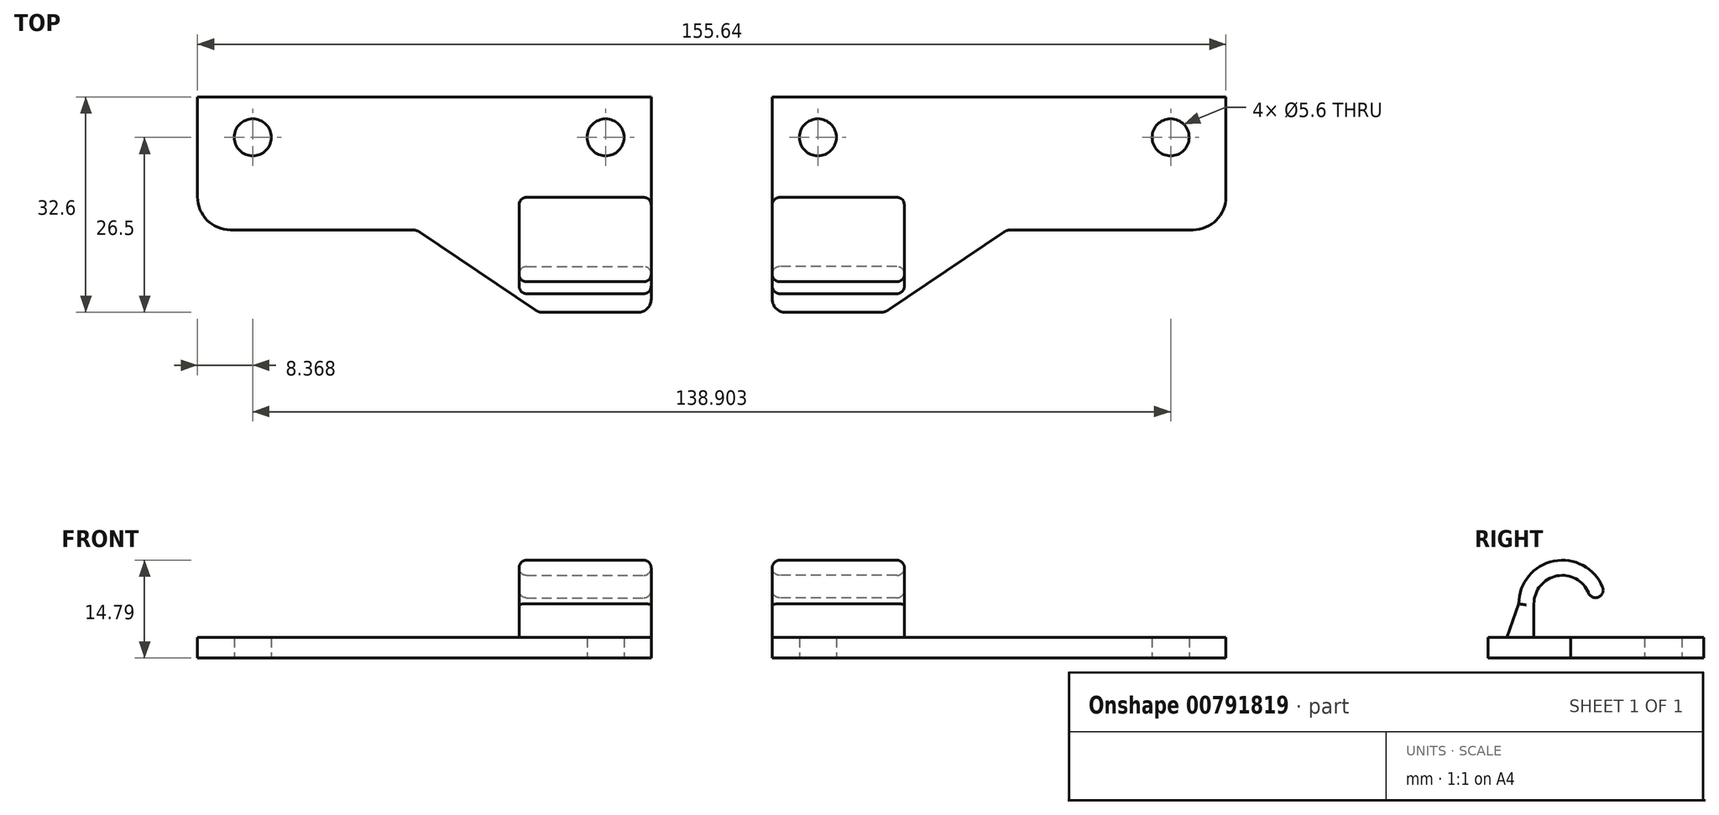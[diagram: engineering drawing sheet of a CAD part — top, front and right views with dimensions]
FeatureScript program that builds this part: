
annotation { "Feature Type Name" : "Feature", "Feature Type Description" : "" }
export const myFeature = defineFeature(function(context is Context, id is Id, definition is map)
    precondition{}
    {
        {
            var Q0;
            Q0=qCreatedBy(makeId("Top.planeOp"),FACE);
            var sketch = newSketch(context, id + "F0", { "sketchPlane" : qUnion([Q0])});
            skCircle(sketch, "E0", {"center": v(-17.35, 21.4) * mm, "radius": 2.8 * mm});
            skLineSegment(sketch, "E1", {"start": v(36.74, 27.5) * mm, "end": v(36.74, 21.3) * mm});
            skCircle(sketch, "E2", {"center": v(36.04, 21.4) * mm, "radius": 2.8 * mm});
            skPoint(sketch, "E3.visualSharp", {"position": v(-25.72, 27.5) * mm});
            skPoint(sketch, "E4.visualSharp", {"position": v(42.94, 27.5) * mm});
            skLineSegment(sketch, "E5", {"start": v(-25.72, 27.5) * mm, "end": v(-25.72, 22.5) * mm});
            skLineSegment(sketch, "E6", {"start": v(-20.72, 27.5) * mm, "end": v(-25.72, 27.5) * mm});
            skPoint(sketch, "E7.visualSharp", {"position": v(-25.72, 7.4) * mm});
            skArc(sketch, "E7.filletArc", {"start": v(-25.72, 12.4) * mm, "mid": v(-24.26, 8.86) * mm, "end": v(-20.72, 7.4) * mm});
            skLineSegment(sketch, "E8", {"start": v(37.94, 27.5) * mm, "end": v(42.94, 27.5) * mm});
            skLineSegment(sketch, "E9", {"start": v(42.94, 22.5) * mm, "end": v(42.94, 27.5) * mm});
            skLineSegment(sketch, "E10", {"start": v(42.94, 7.4) * mm, "end": v(42.94, -3.1) * mm});
            skLineSegment(sketch, "E11", {"start": v(26.55, -5.1) * mm, "end": v(40.94, -5.1) * mm});
            skLineSegment(sketch, "E12", {"start": v(25.43, -4.76) * mm, "end": v(7.9, 7.06) * mm});
            skPoint(sketch, "E13.visualSharp", {"position": v(42.94, -5.1) * mm});
            skArc(sketch, "E13.filletArc", {"start": v(40.94, -5.1) * mm, "mid": v(42.35, -4.51) * mm, "end": v(42.94, -3.1) * mm});
            skPoint(sketch, "E14.visualSharp", {"position": v(25.94, -5.1) * mm});
            skArc(sketch, "E14.filletArc", {"start": v(25.43, -4.76) * mm, "mid": v(25.97, -5.01) * mm, "end": v(26.55, -5.1) * mm});
            skPoint(sketch, "E15.visualSharp", {"position": v(7.4, 7.4) * mm});
            skArc(sketch, "E15.filletArc", {"start": v(7.9, 7.06) * mm, "mid": v(7.36, 7.31) * mm, "end": v(6.78, 7.4) * mm});
            skLineSegment(sketch, "E16", {"start": v(6.78, 7.4) * mm, "end": v(-20.72, 7.4) * mm});
            skLineSegment(sketch, "E17", {"start": v(-20.72, 27.5) * mm, "end": v(37.94, 27.5) * mm});
            skLineSegment(sketch, "E18", {"start": v(-25.72, 22.5) * mm, "end": v(-25.72, 12.4) * mm});
            skLineSegment(sketch, "E19", {"start": v(42.94, 22.5) * mm, "end": v(42.94, 7.4) * mm});
            skSolve(sketch);
        }
        {
            var Q0;
            Q0=qSketchRegion(id+"F0",true);
            extrude(context, id + "F1", {"entities" : qUnion([Q0]), "depth" : 3.1 * mm, "offsetDistance" : 25 * mm});
        }
        {
            var Q0;
            Q0=makeQuery(id+"F1.opExtrude","CAP_FACE",FACE,{"disambiguationData":[OSD([sQuery(id+"F0.wireOp",EDGE,"fae1df17-a2d7-4f6f-ac98-689a16ca2aa0.bottom"),sQuery(id+"F0.wireOp",EDGE,"E0"),sQuery(id+"F0.wireOp",EDGE,"E2"),sQuery(id+"F0.wireOp",EDGE,"F014CPc6-vz4U-GeCE-7854-YxV2qlxx2HBI"),sQuery(id+"F0.wireOp",EDGE,"oqsTX8BA-GUAt-ULMf-udCf-k8zS8YHXaQx7"),sQuery(id+"F0.wireOp",EDGE,"E5"),sQuery(id+"F0.wireOp",EDGE,"E6"),sQuery(id+"F0.wireOp",EDGE,"E7.filletArc"),sQuery(id+"F0.wireOp",EDGE,"E8"),sQuery(id+"F0.wireOp",EDGE,"E9"),sQuery(id+"F0.wireOp",EDGE,"E10"),sQuery(id+"F0.wireOp",EDGE,"E11"),sQuery(id+"F0.wireOp",EDGE,"E12"),sQuery(id+"F0.wireOp",EDGE,"A2VAHK38-QV2u-fNEz-uaTx-NxCy4vqKou6f"),sQuery(id+"F0.wireOp",EDGE,"E13.filletArc"),sQuery(id+"F0.wireOp",EDGE,"E14.filletArc"),sQuery(id+"F0.wireOp",EDGE,"E15.filletArc")])],"isStart":false});
            var sketch = newSketch(context, id + "F2", { "sketchPlane" : qUnion([Q0])});
            skLineSegment(sketch, "E20.bottom", {"start": v(22.94, 1.84) * mm, "end": v(42.94, 1.84) * mm});
            skLineSegment(sketch, "E20.top", {"start": v(22.94, -0.46) * mm, "end": v(42.94, -0.46) * mm});
            skLineSegment(sketch, "E20.left", {"start": v(22.94, 1.84) * mm, "end": v(22.94, -0.46) * mm});
            skLineSegment(sketch, "E20.right", {"start": v(42.94, 1.84) * mm, "end": v(42.94, -0.46) * mm});
            skSolve(sketch);
        }
        {
            var Q0;
            Q0=qSketchRegion(id+"F2",true);
            extrude(context, id + "F3", {"entities" : qUnion([Q0]), "operationType" : NewBodyOperationType.ADD, "depth" : 5.1 * mm, "offsetDistance" : 25 * mm});
        }
        {
            var Q0;
            Q0=makeQuery(id+"F3.opExtrude","CAP_FACE",FACE,{"disambiguationData":[OSD([sQuery(id+"F2.wireOp",EDGE,"E20.bottom"),sQuery(id+"F2.wireOp",EDGE,"E20.top"),sQuery(id+"F2.wireOp",EDGE,"E20.left"),sQuery(id+"F2.wireOp",EDGE,"E20.right")])],"isStart":false});
            var sketch = newSketch(context, id + "F4", { "sketchPlane" : qUnion([Q0])});
            skLineSegment(sketch, "E21", {"start": v(22.94, 6.13) * mm, "end": v(42.94, 6.13) * mm});
            skSolve(sketch);
        }
        {
            var Q0;
            Q0=makeQuery(id+"F3.opExtrude","CAP_FACE",FACE,{"disambiguationData":[OSD([sQuery(id+"F2.wireOp",EDGE,"E20.bottom"),sQuery(id+"F2.wireOp",EDGE,"E20.top"),sQuery(id+"F2.wireOp",EDGE,"E20.left"),sQuery(id+"F2.wireOp",EDGE,"E20.right")])],"isStart":false});
            var Q1;
            Q1=sQuery(id+"F4.wireOp",EDGE,"E21");
            revolve(context, id + "F5", {"operationType" : NewBodyOperationType.ADD, "surfaceOperationType" : NewSurfaceOperationType.NEW, "entities" : qUnion([Q0]), "axis" : qUnion([Q1]), "revolveType" : RevolveType.ONE_DIRECTION, "oppositeDirection" : true, "angle" : 170 * degree});
        }
        {
            var Q0;
            Q0=makeQuery(id+"F5.opRevolve","CAP_EDGE",EDGE,{"disambiguationData":[OSD([sQuery(id+"F2.wireOp",EDGE,"E20.bottom")])],"isStart":false});
            var Q1;
            Q1=makeQuery(id+"F5.opRevolve","CAP_EDGE",EDGE,{"disambiguationData":[OSD([sQuery(id+"F2.wireOp",EDGE,"E20.top")])],"isStart":false});
            fillet(context, id + "F6", {"entities" : qUnion([Q0, Q1]), "radius" : 1.15 * mm, "tangentPropagation" : true, "allowEdgeOverflow" : false});
        }
        {
            var Q0;
            {var subQ0=sQuery(id+"F2.wireOp",EDGE,"E20.left");Q0=makeQuery(id+"F5.boolean.opBoolean","MERGE",FACE,{"derivedFrom":[makeQuery(id+"F3.opExtrude","SWEPT_FACE",FACE,{"disambiguationData":[OSD([subQ0])]}),makeQuery(id+"F5.opRevolve","SWEPT_FACE",FACE,{"disambiguationData":[OSD([subQ0])]})]});}
            var sketch = newSketch(context, id + "F7", { "sketchPlane" : qUnion([Q0])});
            skLineSegment(sketch, "E22", {"start": v(0.46, 8.2) * mm, "end": v(2.26, 3.1) * mm});
            skLineSegment(sketch, "E23", {"start": v(2.26, 3.1) * mm, "end": v(0.46, 3.1) * mm});
            skLineSegment(sketch, "E24", {"start": v(0.46, 8.2) * mm, "end": v(0.46, 3.1) * mm});
            skSolve(sketch);
        }
        {
            var Q0;
            Q0=qSketchRegion(id+"F7",true);
            extrude(context, id + "F8", {"entities" : qUnion([Q0]), "operationType" : NewBodyOperationType.ADD, "oppositeDirection" : true, "depth" : 20 * mm, "offsetDistance" : 25 * mm});
        }
        {
            var Q0;
            Q0=makeQuery(id+"F8.opExtrude","CAP_EDGE",EDGE,{"disambiguationData":[OSD([sQuery(id+"F7.wireOp",EDGE,"E22")])],"isStart":true});
            var Q1;
            Q1=makeQuery(id+"F5.opRevolve","SWEPT_EDGE",EDGE,{"disambiguationData":[OSD([sQuery(id+"F2.wireOp",EDGE,"E20.top"),sQuery(id+"F2.wireOp",EDGE,"E20.left")])]});
            var Q2;
            Q2=makeQuery(id+"F8.opExtrude","CAP_EDGE",EDGE,{"disambiguationData":[OSD([sQuery(id+"F7.wireOp",EDGE,"E22")])],"isStart":false});
            var Q3;
            Q3=makeQuery(id+"F5.opRevolve","SWEPT_EDGE",EDGE,{"disambiguationData":[OSD([sQuery(id+"F2.wireOp",EDGE,"E20.top"),sQuery(id+"F2.wireOp",EDGE,"E20.right")])]});
            fillet(context, id + "F9", {"entities" : qUnion([Q0, Q1, Q2, Q3]), "radius" : 1.14 * mm, "tangentPropagation" : true, "allowEdgeOverflow" : false});
        }
        {
            var Q0;
            Q0=makeQuery(id+"F1.opExtrude","SWEPT_BODY",BODY,{"disambiguationData":[OSD([sQuery(id+"F0.wireOp",EDGE,"fae1df17-a2d7-4f6f-ac98-689a16ca2aa0.bottom"),sQuery(id+"F0.wireOp",EDGE,"E0"),sQuery(id+"F0.wireOp",EDGE,"E2"),sQuery(id+"F0.wireOp",EDGE,"F014CPc6-vz4U-GeCE-7854-YxV2qlxx2HBI"),sQuery(id+"F0.wireOp",EDGE,"oqsTX8BA-GUAt-ULMf-udCf-k8zS8YHXaQx7"),sQuery(id+"F0.wireOp",EDGE,"E5"),sQuery(id+"F0.wireOp",EDGE,"E6"),sQuery(id+"F0.wireOp",EDGE,"E7.filletArc"),sQuery(id+"F0.wireOp",EDGE,"E8"),sQuery(id+"F0.wireOp",EDGE,"E9"),sQuery(id+"F0.wireOp",EDGE,"E10"),sQuery(id+"F0.wireOp",EDGE,"E11"),sQuery(id+"F0.wireOp",EDGE,"E12"),sQuery(id+"F0.wireOp",EDGE,"A2VAHK38-QV2u-fNEz-uaTx-NxCy4vqKou6f"),sQuery(id+"F0.wireOp",EDGE,"E13.filletArc"),sQuery(id+"F0.wireOp",EDGE,"E14.filletArc"),sQuery(id+"F0.wireOp",EDGE,"E15.filletArc")])]});
            transform(context, id + "F10", {"entities" : qUnion([Q0]), "transformType" : TransformType.TRANSLATION_3D, "dx" : -52.1 * mm, "dy" : 0 * mm, "dz" : 0 * mm, "makeCopy" : false});
        }
        {
            var Q0;
            Q0=makeQuery(id+"F1.opExtrude","SWEPT_BODY",BODY,{"disambiguationData":[OSD([sQuery(id+"F0.wireOp",EDGE,"fae1df17-a2d7-4f6f-ac98-689a16ca2aa0.bottom"),sQuery(id+"F0.wireOp",EDGE,"E0"),sQuery(id+"F0.wireOp",EDGE,"E2"),sQuery(id+"F0.wireOp",EDGE,"F014CPc6-vz4U-GeCE-7854-YxV2qlxx2HBI"),sQuery(id+"F0.wireOp",EDGE,"oqsTX8BA-GUAt-ULMf-udCf-k8zS8YHXaQx7"),sQuery(id+"F0.wireOp",EDGE,"E5"),sQuery(id+"F0.wireOp",EDGE,"E6"),sQuery(id+"F0.wireOp",EDGE,"E7.filletArc"),sQuery(id+"F0.wireOp",EDGE,"E8"),sQuery(id+"F0.wireOp",EDGE,"E9"),sQuery(id+"F0.wireOp",EDGE,"E10"),sQuery(id+"F0.wireOp",EDGE,"E11"),sQuery(id+"F0.wireOp",EDGE,"E12"),sQuery(id+"F0.wireOp",EDGE,"A2VAHK38-QV2u-fNEz-uaTx-NxCy4vqKou6f"),sQuery(id+"F0.wireOp",EDGE,"E13.filletArc"),sQuery(id+"F0.wireOp",EDGE,"E14.filletArc"),sQuery(id+"F0.wireOp",EDGE,"E15.filletArc")])]});
            var Q1;
            Q1=qCreatedBy(makeId("Right.planeOp"),FACE);
            mirror(context, id + "F11", {"entities" : qUnion([Q0]), "mirrorPlane" : qUnion([Q1])});
        }
    });
